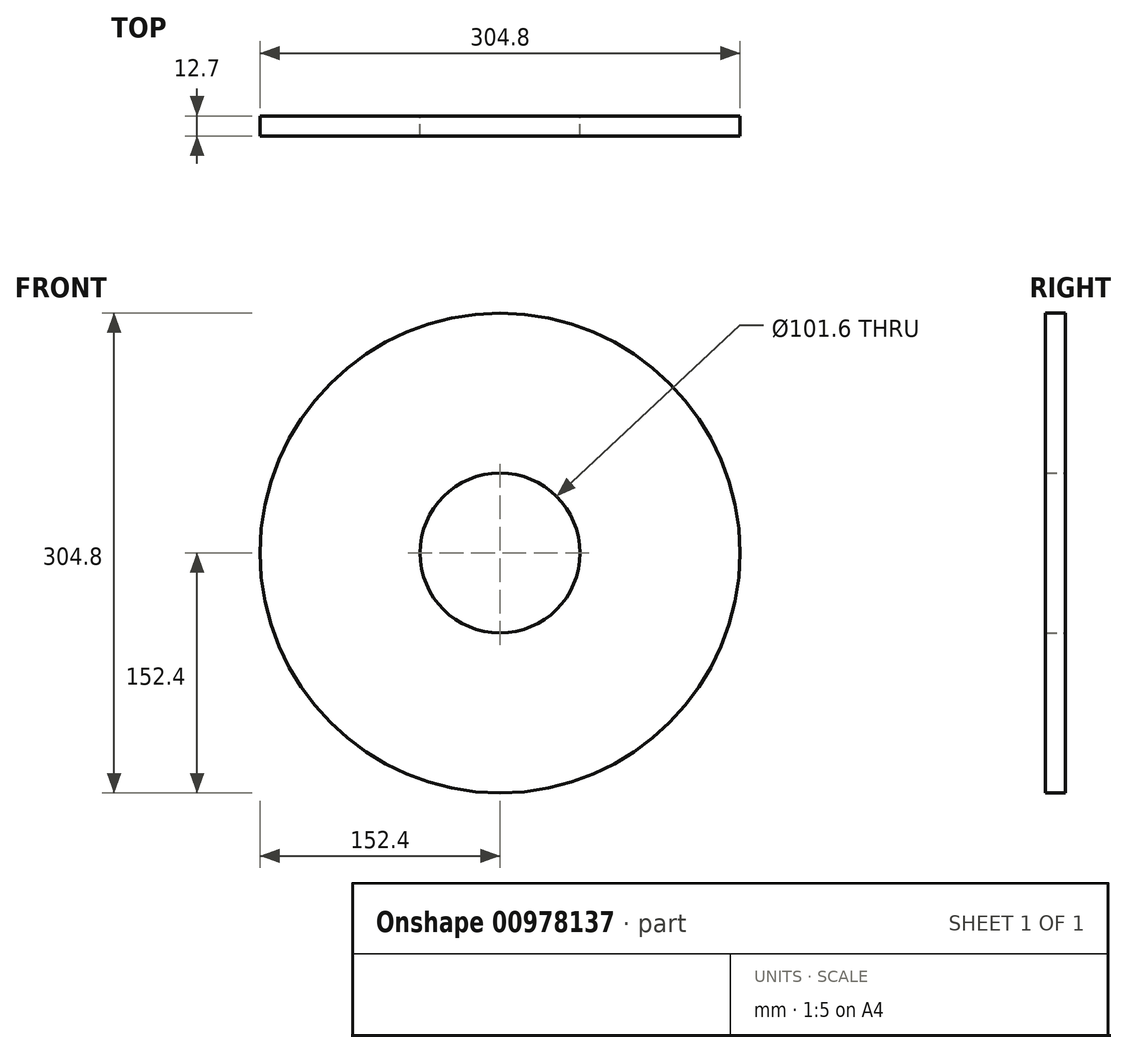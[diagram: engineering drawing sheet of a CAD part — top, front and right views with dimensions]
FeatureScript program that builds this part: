
annotation { "Feature Type Name" : "Feature", "Feature Type Description" : "" }
export const myFeature = defineFeature(function(context is Context, id is Id, definition is map)
    precondition{}
    {
        {
            var Q0;
            Q0=qCreatedBy(makeId("Front.planeOp"),FACE);
            var sketch = newSketch(context, id + "F0", { "sketchPlane" : qUnion([Q0])});
            skCircle(sketch, "E0", {"center": v(0, 0) * mm, "radius": 152.4 * mm});
            skCircle(sketch, "E1", {"center": v(0, 0) * mm, "radius": 50.8 * mm});
            skSolve(sketch);
        }
        {
            var Q0;
            Q0=makeQuery(id+"F0.imprint","IMPRINT",FACE,{"disambiguationData":[TD([[makeQuery(id+"F0.imprint","IMPRINT",EDGE,{"derivedFrom":sQuery(id+"F0.wireOp",EDGE,"E0")}),1.0]])]});
            extrude(context, id + "F1", {"entities" : qUnion([Q0]), "depth" : 12.7 * mm, "offsetDistance" : 25.4 * mm});
        }
    });
